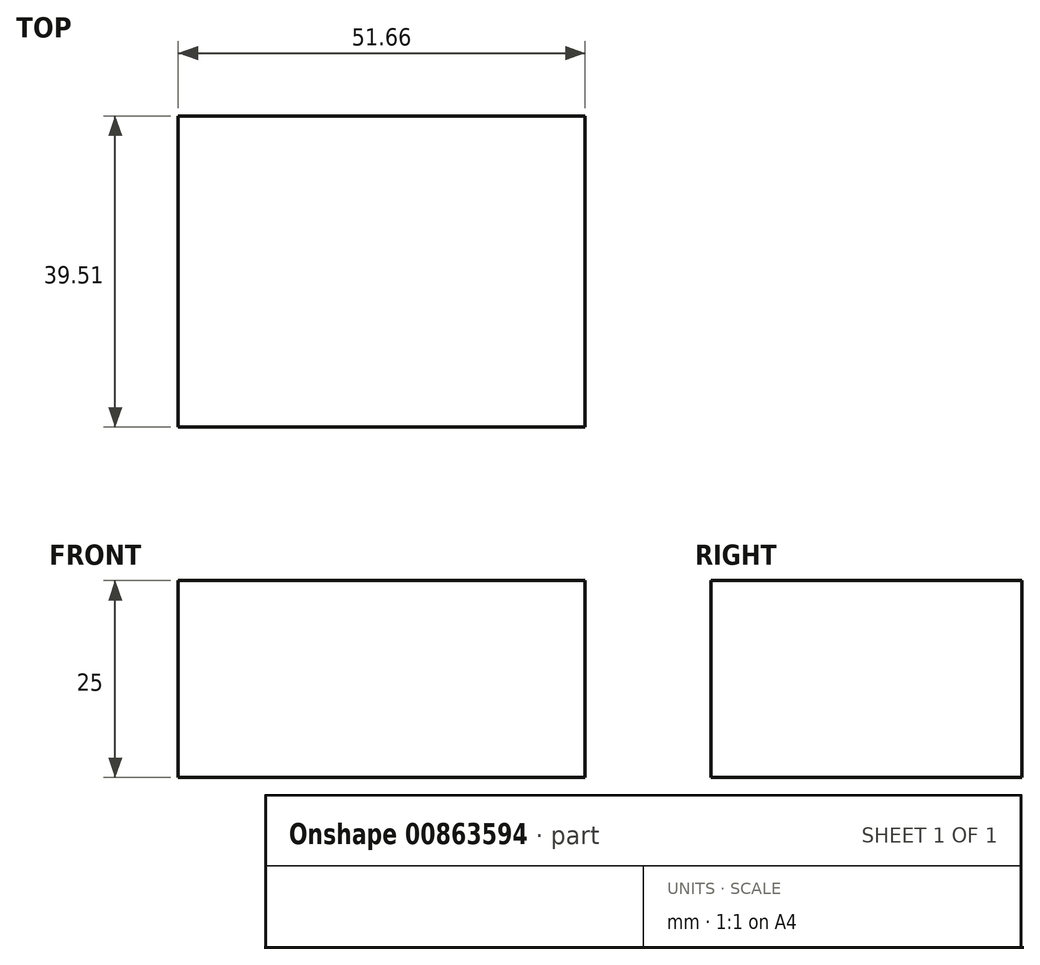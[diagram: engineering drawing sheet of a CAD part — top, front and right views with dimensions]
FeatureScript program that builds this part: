
annotation { "Feature Type Name" : "Feature", "Feature Type Description" : "" }
export const myFeature = defineFeature(function(context is Context, id is Id, definition is map)
    precondition{}
    {
        {
            var Q0;
            Q0=qCreatedBy(makeId("Top.planeOp"),FACE);
            var sketch = newSketch(context, id + "F0", { "sketchPlane" : qUnion([Q0])});
            skLineSegment(sketch, "E0.bottom", {"start": v(71.82, 68.96) * mm, "end": v(123.48, 68.96) * mm});
            skLineSegment(sketch, "E0.top", {"start": v(71.82, 29.45) * mm, "end": v(123.48, 29.45) * mm});
            skLineSegment(sketch, "E0.left", {"start": v(71.82, 68.96) * mm, "end": v(71.82, 29.45) * mm});
            skLineSegment(sketch, "E0.right", {"start": v(123.48, 68.96) * mm, "end": v(123.48, 29.45) * mm});
            skSolve(sketch);
        }
        {
            var Q0;
            Q0=makeQuery(id+"F0.imprint","IMPRINT",FACE,{"disambiguationData":[TD([[makeQuery(id+"F0.imprint","IMPRINT",EDGE,{"derivedFrom":sQuery(id+"F0.wireOp",EDGE,"E0.bottom")}),-1.0]])]});
            extrude(context, id + "F1", {"entities" : qUnion([Q0]), "depth" : 25 * mm, "offsetDistance" : 25 * mm});
        }
    });
